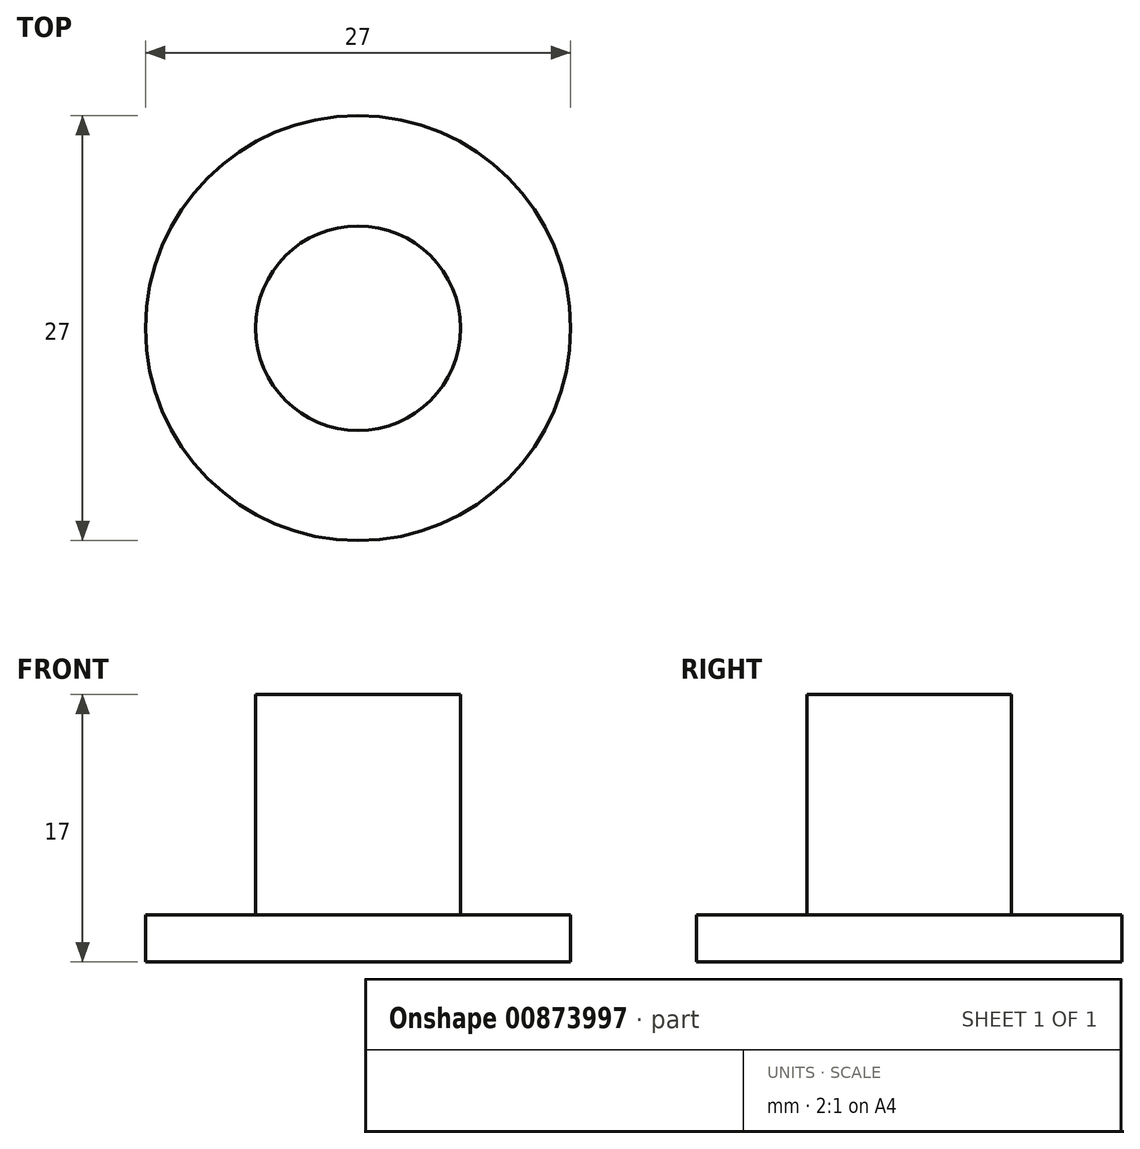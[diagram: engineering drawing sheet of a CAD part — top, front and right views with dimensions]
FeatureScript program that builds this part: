
annotation { "Feature Type Name" : "Feature", "Feature Type Description" : "" }
export const myFeature = defineFeature(function(context is Context, id is Id, definition is map)
    precondition{}
    {
        {
            var Q0;
            Q0=qCreatedBy(makeId("Top.planeOp"),FACE);
            var sketch = newSketch(context, id + "F0", { "sketchPlane" : qUnion([Q0])});
            skCircle(sketch, "E0", {"center": v(0, 0) * mm, "radius": 13.5 * mm});
            skCircle(sketch, "E1", {"center": v(0, 0) * mm, "radius": 6.5 * mm});
            skSolve(sketch);
        }
        {
            var Q0;
            Q0=makeQuery(id+"F0.imprint","IMPRINT",FACE,{"disambiguationData":[TD([[makeQuery(id+"F0.imprint","IMPRINT",EDGE,{"derivedFrom":sQuery(id+"F0.wireOp",EDGE,"E1")}),1.0]])]});
            extrude(context, id + "F1", {"entities" : qUnion([Q0]), "depth" : 17 * mm, "offsetDistance" : 25 * mm});
        }
        {
            var Q0;
            Q0=qSketchRegion(id+"F0",true);
            extrude(context, id + "F2", {"entities" : qUnion([Q0]), "operationType" : NewBodyOperationType.ADD, "depth" : 3 * mm, "offsetDistance" : 25 * mm});
        }
    });
